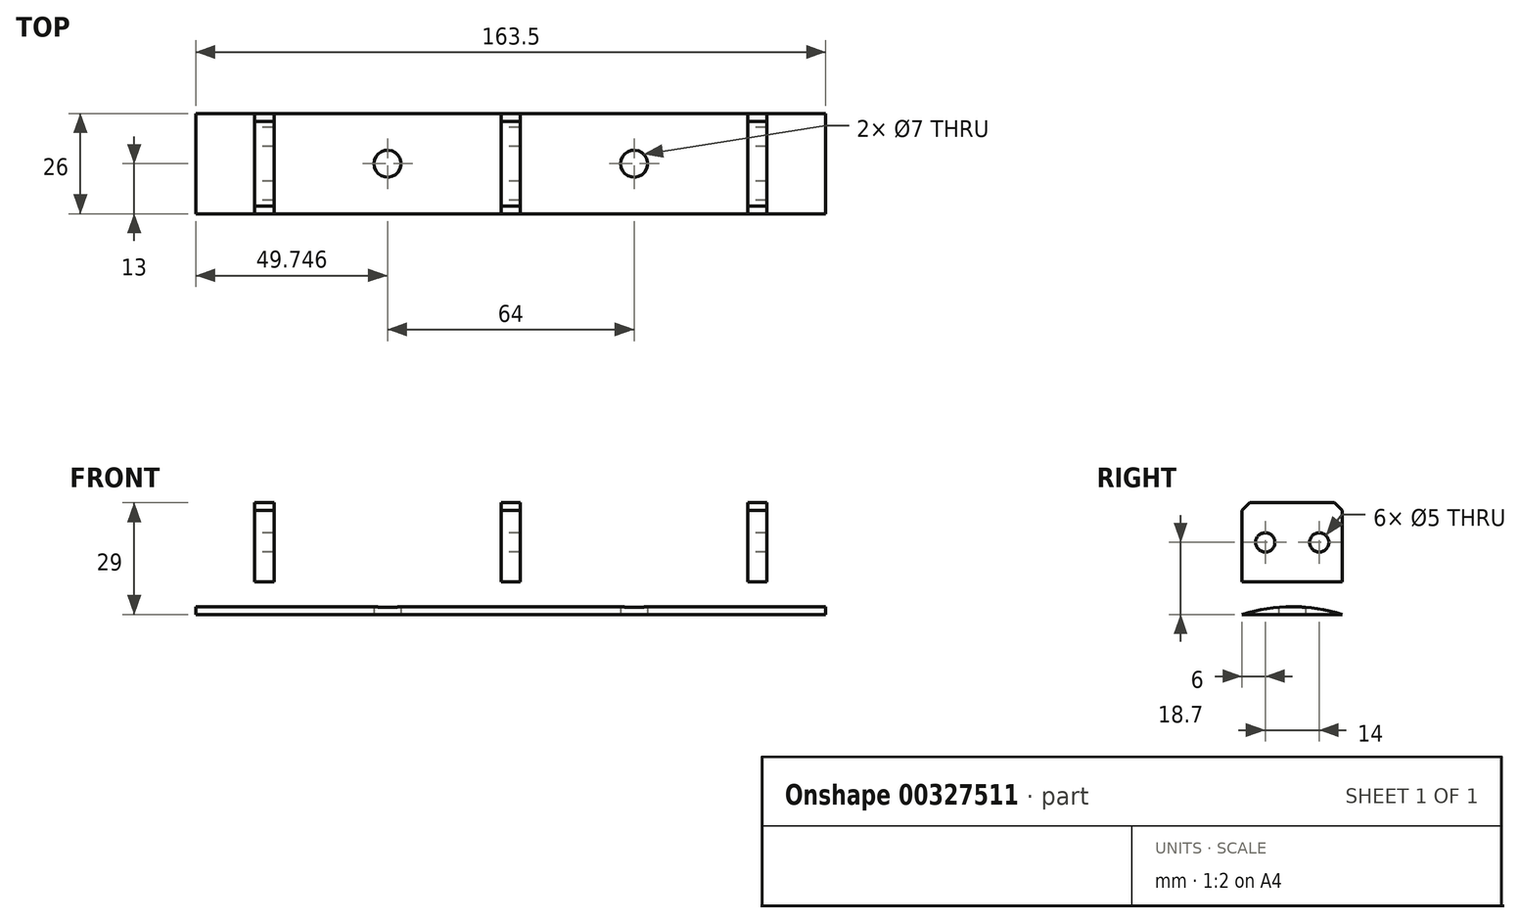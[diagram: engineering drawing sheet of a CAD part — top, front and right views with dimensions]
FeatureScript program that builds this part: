
annotation { "Feature Type Name" : "Feature", "Feature Type Description" : "" }
export const myFeature = defineFeature(function(context is Context, id is Id, definition is map)
    precondition{}
    {
        {
            var Q0;
            Q0=qCreatedBy(makeId("Front.planeOp"),FACE);
            var sketch = newSketch(context, id + "F0", { "sketchPlane" : qUnion([Q0])});
            skLineSegment(sketch, "E0.bottom", {"start": v(-71.23, 0) * mm, "end": v(92.27, 0) * mm});
            skLineSegment(sketch, "E0.top", {"start": v(-71.23, 8.5) * mm, "end": v(-55.98, 8.5) * mm});
            skLineSegment(sketch, "E0.left", {"start": v(-71.23, 0) * mm, "end": v(-71.23, 8.5) * mm});
            skLineSegment(sketch, "E0.right", {"start": v(92.27, 0) * mm, "end": v(92.27, 8.5) * mm});
            skLineSegment(sketch, "E1.top", {"start": v(-55.98, 29) * mm, "end": v(-50.98, 29) * mm});
            skLineSegment(sketch, "E1.left", {"start": v(-55.98, 8.5) * mm, "end": v(-55.98, 29) * mm});
            skLineSegment(sketch, "E1.right", {"start": v(-50.98, 8.5) * mm, "end": v(-50.98, 29) * mm});
            skLineSegment(sketch, "E2.top", {"start": v(8.02, 29) * mm, "end": v(13.02, 29) * mm});
            skLineSegment(sketch, "E2.left", {"start": v(8.02, 8.5) * mm, "end": v(8.02, 29) * mm});
            skLineSegment(sketch, "E2.right", {"start": v(13.02, 8.5) * mm, "end": v(13.02, 29) * mm});
            skLineSegment(sketch, "E3.top", {"start": v(72.02, 29) * mm, "end": v(77.02, 29) * mm});
            skLineSegment(sketch, "E3.left", {"start": v(72.02, 8.5) * mm, "end": v(72.02, 29) * mm});
            skLineSegment(sketch, "E3.right", {"start": v(77.02, 8.5) * mm, "end": v(77.02, 29) * mm});
            skLineSegment(sketch, "E4.trimOffspring", {"start": v(-50.98, 8.5) * mm, "end": v(8.02, 8.5) * mm});
            skLineSegment(sketch, "E5.trimOffspring", {"start": v(13.02, 8.5) * mm, "end": v(72.02, 8.5) * mm});
            skLineSegment(sketch, "E6.trimOffspring", {"start": v(77.02, 8.5) * mm, "end": v(92.27, 8.5) * mm});
            skSolve(sketch);
        }
        {
            var Q0;
            Q0=makeQuery(id+"F0.imprint","IMPRINT",FACE,{"disambiguationData":[TD([[makeQuery(id+"F0.imprint","IMPRINT",EDGE,{"derivedFrom":sQuery(id+"F0.wireOp",EDGE,"E0.bottom")}),1.0]])]});
            var Q1;
            Q1=makeQuery(id+"F0.imprint","IMPRINT",FACE,{"disambiguationData":[TD([[makeQuery(id+"F0.imprint","IMPRINT",EDGE,{"derivedFrom":sQuery(id+"F0.wireOp",EDGE,"E3.top")}),-1.0]])]});
            extrude(context, id + "F1", {"entities" : qUnion([Q0, Q1]), "depth" : 26 * mm});
        }
        {
            var Q0;
            Q0=makeQuery(id+"F1.opExtrude","SWEPT_FACE",FACE,{"disambiguationData":[OSD([sQuery(id+"F0.wireOp",EDGE,"E0.right")])]});
            var sketch = newSketch(context, id + "F2", { "sketchPlane" : qUnion([Q0])});
            skLineSegment(sketch, "E7.0", {"start": v(-26, 8.5) * mm, "end": v(-26, 29) * mm});
            skLineSegment(sketch, "E8.0", {"start": v(0, 8.5) * mm, "end": v(0, 29) * mm});
            skLineSegment(sketch, "E9.0.1", {"start": v(0, 29) * mm, "end": v(-26, 29) * mm});
            skLineSegment(sketch, "E9.0.2", {"start": v(-26, 29) * mm, "end": v(-26, 8.5) * mm});
            skLineSegment(sketch, "E9.0.3", {"start": v(-26, 8.5) * mm, "end": v(0, 8.5) * mm});
            skLineSegment(sketch, "E10.0.0", {"start": v(0, 0) * mm, "end": v(0, 8.5) * mm});
            skLineSegment(sketch, "E10.0.1", {"start": v(0, 8.5) * mm, "end": v(-26, 8.5) * mm});
            skLineSegment(sketch, "E10.0.2", {"start": v(-26, 8.5) * mm, "end": v(-26, 0) * mm});
            skLineSegment(sketch, "E10.0.3", {"start": v(-26, 0) * mm, "end": v(-13, 0) * mm});
            skLineSegment(sketch, "E11", {"start": v(-13, 0) * mm, "end": v(-13, -49.65) * mm});
            skLineSegment(sketch, "E12", {"start": v(-26, 0) * mm, "end": v(-13, -41.51) * mm});
            skLineSegment(sketch, "E13", {"start": v(-13, -41.51) * mm, "end": v(0, 0) * mm});
            skArc(sketch, "E14", {"start": v(-26, 0) * mm, "mid": v(-13, 1.99) * mm, "end": v(0, 0) * mm});
            skLineSegment(sketch, "E15.0", {"start": v(-26, 0) * mm, "end": v(0, 0) * mm});
            skLineSegment(sketch, "E16", {"start": v(-13, 0) * mm, "end": v(-13, 18.7) * mm});
            skLineSegment(sketch, "E17", {"start": v(-13, 18.7) * mm, "end": v(-20, 18.7) * mm});
            skLineSegment(sketch, "E18", {"start": v(-13, 18.7) * mm, "end": v(-6, 18.7) * mm});
            skSolve(sketch);
        }
        {
            var Q0;
            {var subQ0=sQuery(id+"F2.wireOp",EDGE,"E14");Q0=makeQuery(id+"F2.imprint","IMPRINT",FACE,{"disambiguationData":[TD([[makeQuery(id+"F2.imprint","IMPRINT",EDGE,{"derivedFrom":subQ0}),-1.0]])]});}
            extrude(context, id + "F3", {"entities" : qUnion([Q0]), "operationType" : NewBodyOperationType.REMOVE, "oppositeDirection" : true, "depth" : 200 * mm});
        }
        {
            var Q0;
            Q0=makeQuery(id+"F1.opExtrude","CAP_EDGE",EDGE,{"disambiguationData":[OSD([sQuery(id+"F0.wireOp",EDGE,"E3.top")])],"isStart":true});
            var Q1;
            Q1=makeQuery(id+"F1.opExtrude","CAP_EDGE",EDGE,{"disambiguationData":[OSD([sQuery(id+"F0.wireOp",EDGE,"E3.top")])],"isStart":false});
            var Q2;
            Q2=makeQuery(id+"F1.opExtrude","CAP_EDGE",EDGE,{"disambiguationData":[OSD([sQuery(id+"F0.wireOp",EDGE,"E2.top")])],"isStart":false});
            var Q3;
            Q3=makeQuery(id+"F1.opExtrude","CAP_EDGE",EDGE,{"disambiguationData":[OSD([sQuery(id+"F0.wireOp",EDGE,"E2.top")])],"isStart":true});
            var Q4;
            Q4=makeQuery(id+"F1.opExtrude","CAP_EDGE",EDGE,{"disambiguationData":[OSD([sQuery(id+"F0.wireOp",EDGE,"E1.top")])],"isStart":false});
            var Q5;
            Q5=makeQuery(id+"F1.opExtrude","CAP_EDGE",EDGE,{"disambiguationData":[OSD([sQuery(id+"F0.wireOp",EDGE,"E1.top")])],"isStart":true});
            chamfer(context, id + "F4", {"entities" : qUnion([Q0, Q1, Q2, Q3, Q4, Q5]), "chamferType" : ChamferType.OFFSET_ANGLE, "width" : 2 * mm, "oppositeDirection" : false, "angle" : 45 * degree, "tangentPropagation" : true});
        }
        {
            var Q0;
            Q0=sQuery(id+"F2.wireOp",VERTEX,"E17.end");
            var Q1;
            Q1=sQuery(id+"F2.wireOp",VERTEX,"E18.end");
            var Q2;
            Q2=makeQuery(id+"F1.opExtrude","SWEPT_BODY",BODY,{"disambiguationData":[OSD([sQuery(id+"F0.wireOp",EDGE,"E0.bottom"),sQuery(id+"F0.wireOp",EDGE,"E0.top"),sQuery(id+"F0.wireOp",EDGE,"E0.left"),sQuery(id+"F0.wireOp",EDGE,"E0.right"),sQuery(id+"F0.wireOp",EDGE,"E1.top"),sQuery(id+"F0.wireOp",EDGE,"E1.left"),sQuery(id+"F0.wireOp",EDGE,"E1.right"),sQuery(id+"F0.wireOp",EDGE,"E2.top"),sQuery(id+"F0.wireOp",EDGE,"E2.left"),sQuery(id+"F0.wireOp",EDGE,"E2.right"),sQuery(id+"F0.wireOp",EDGE,"E3.top"),sQuery(id+"F0.wireOp",EDGE,"E3.left"),sQuery(id+"F0.wireOp",EDGE,"E3.right"),sQuery(id+"F0.wireOp",EDGE,"E4.trimOffspring"),sQuery(id+"F0.wireOp",EDGE,"E5.trimOffspring"),sQuery(id+"F0.wireOp",EDGE,"E6.trimOffspring")])]});
            hole(context, id + "F5", {"style" : HoleStyle.SIMPLE, "endStyle" : HoleEndStyle.BLIND, "holeDiameter" : 5 * mm, "holeDepth" : 300 * mm, "tappedDepth" : 12 * mm, "tapClearance" : 3, "locations" : qUnion([Q0, Q1]), "scope" : qUnion([Q2]), "startStyle" : HoleStartStyle.PART});
        }
        {
            var Q0;
            Q0=makeQuery(id+"F1.opExtrude","CAP_VERTEX",VERTEX,{"disambiguationData":[OSD([sQuery(id+"F0.wireOp",EDGE,"E2.right"),sQuery(id+"F0.wireOp",EDGE,"E5.trimOffspring")])],"isStart":false});
            var Q1;
            Q1=makeQuery(id+"F1.opExtrude","CAP_VERTEX",VERTEX,{"disambiguationData":[OSD([sQuery(id+"F0.wireOp",EDGE,"E2.right"),sQuery(id+"F0.wireOp",EDGE,"E5.trimOffspring")])],"isStart":true});
            var Q2;
            Q2=makeQuery(id+"F1.opExtrude","CAP_VERTEX",VERTEX,{"disambiguationData":[OSD([sQuery(id+"F0.wireOp",EDGE,"E2.left"),sQuery(id+"F0.wireOp",EDGE,"E4.trimOffspring")])],"isStart":false});
            cPlane(context, id + "F6", {"entities" : qUnion([Q0, Q1, Q2]), "cplaneType" : CPlaneType.THREE_POINT, "offset" : 25 * mm, "width" : 150 * mm, "height" : 150 * mm});
        }
        {
            var Q0;
            Q0=qCreatedBy(id+"F6.planeOp",FACE);
            var sketch = newSketch(context, id + "F7", { "sketchPlane" : qUnion([Q0])});
            skPoint(sketch, "E19.0", {"position": v(10.52, 26) * mm});
            skLineSegment(sketch, "E20", {"start": v(10.52, 26) * mm, "end": v(10.52, 13) * mm});
            skLineSegment(sketch, "E21", {"start": v(10.52, 13) * mm, "end": v(42.52, 13) * mm});
            skLineSegment(sketch, "E22", {"start": v(10.52, 13) * mm, "end": v(-21.48, 13) * mm});
            skSolve(sketch);
        }
        {
            var Q0;
            Q0=sQuery(id+"F7.wireOp",VERTEX,"E22.end");
            var Q1;
            Q1=sQuery(id+"F7.wireOp",VERTEX,"E21.end");
            var Q2;
            Q2=makeQuery(id+"F1.opExtrude","SWEPT_BODY",BODY,{"disambiguationData":[OSD([sQuery(id+"F0.wireOp",EDGE,"E0.bottom"),sQuery(id+"F0.wireOp",EDGE,"E0.top"),sQuery(id+"F0.wireOp",EDGE,"E0.left"),sQuery(id+"F0.wireOp",EDGE,"E0.right"),sQuery(id+"F0.wireOp",EDGE,"E1.top"),sQuery(id+"F0.wireOp",EDGE,"E1.left"),sQuery(id+"F0.wireOp",EDGE,"E1.right"),sQuery(id+"F0.wireOp",EDGE,"E2.top"),sQuery(id+"F0.wireOp",EDGE,"E2.left"),sQuery(id+"F0.wireOp",EDGE,"E2.right"),sQuery(id+"F0.wireOp",EDGE,"E3.top"),sQuery(id+"F0.wireOp",EDGE,"E3.left"),sQuery(id+"F0.wireOp",EDGE,"E3.right"),sQuery(id+"F0.wireOp",EDGE,"E4.trimOffspring"),sQuery(id+"F0.wireOp",EDGE,"E5.trimOffspring"),sQuery(id+"F0.wireOp",EDGE,"E6.trimOffspring")])]});
            hole(context, id + "F8", {"style" : HoleStyle.SIMPLE, "endStyle" : HoleEndStyle.BLIND, "oppositeDirection" : true, "holeDiameter" : 7 * mm, "holeDepth" : 300 * mm, "tappedDepth" : 12 * mm, "tapClearance" : 3, "locations" : qUnion([Q0, Q1]), "scope" : qUnion([Q2]), "startStyle" : HoleStartStyle.PART});
        }
    });
